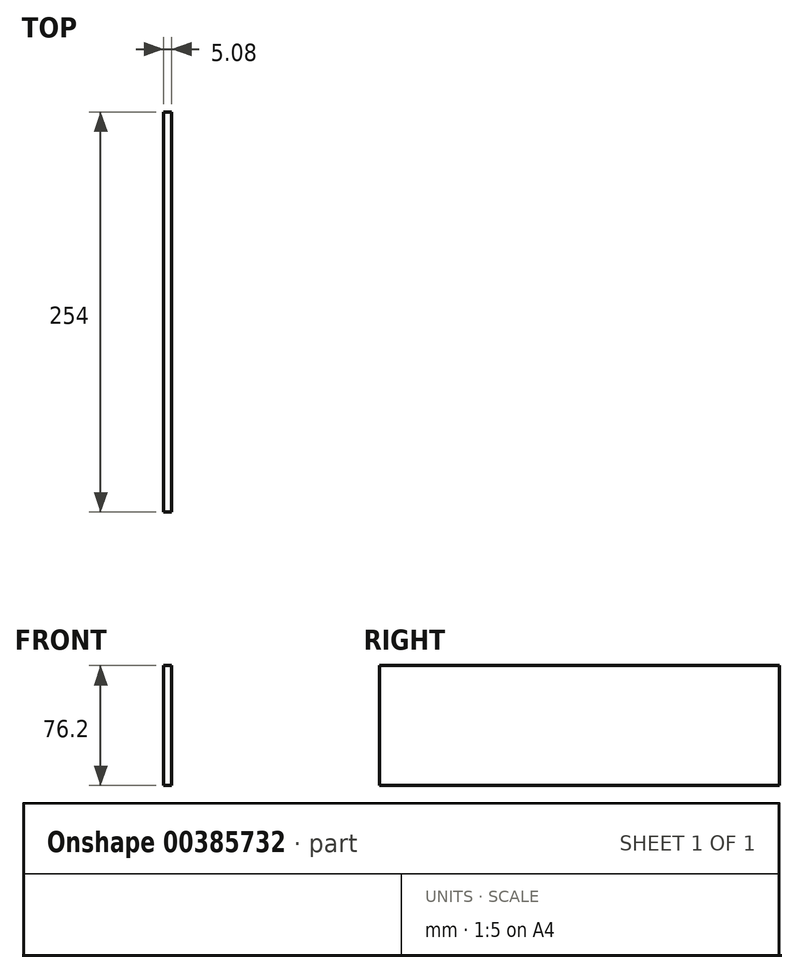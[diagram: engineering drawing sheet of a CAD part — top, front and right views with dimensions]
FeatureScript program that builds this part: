
annotation { "Feature Type Name" : "Feature", "Feature Type Description" : "" }
export const myFeature = defineFeature(function(context is Context, id is Id, definition is map)
    precondition{}
    {
        {
            var Q0;
            Q0=qCreatedBy(makeId("Front.planeOp"),FACE);
            var sketch = newSketch(context, id + "F0", { "sketchPlane" : qUnion([Q0])});
            skLineSegment(sketch, "E0.bottom", {"start": v(-2.54, 38.1) * mm, "end": v(2.54, 38.1) * mm});
            skLineSegment(sketch, "E0.top", {"start": v(-2.54, -38.1) * mm, "end": v(2.54, -38.1) * mm});
            skLineSegment(sketch, "E0.left", {"start": v(-2.54, 38.1) * mm, "end": v(-2.54, -38.1) * mm});
            skLineSegment(sketch, "E0.right", {"start": v(2.54, 38.1) * mm, "end": v(2.54, -38.1) * mm});
            skPoint(sketch, "E0.middle", {"position": v(0, 0) * mm});
            skSolve(sketch);
        }
        {
            var Q0;
            Q0=qSketchRegion(id+"F0",true);
            extrude(context, id + "F1", {"entities" : qUnion([Q0]), "depth" : 254 * mm});
        }
    });
